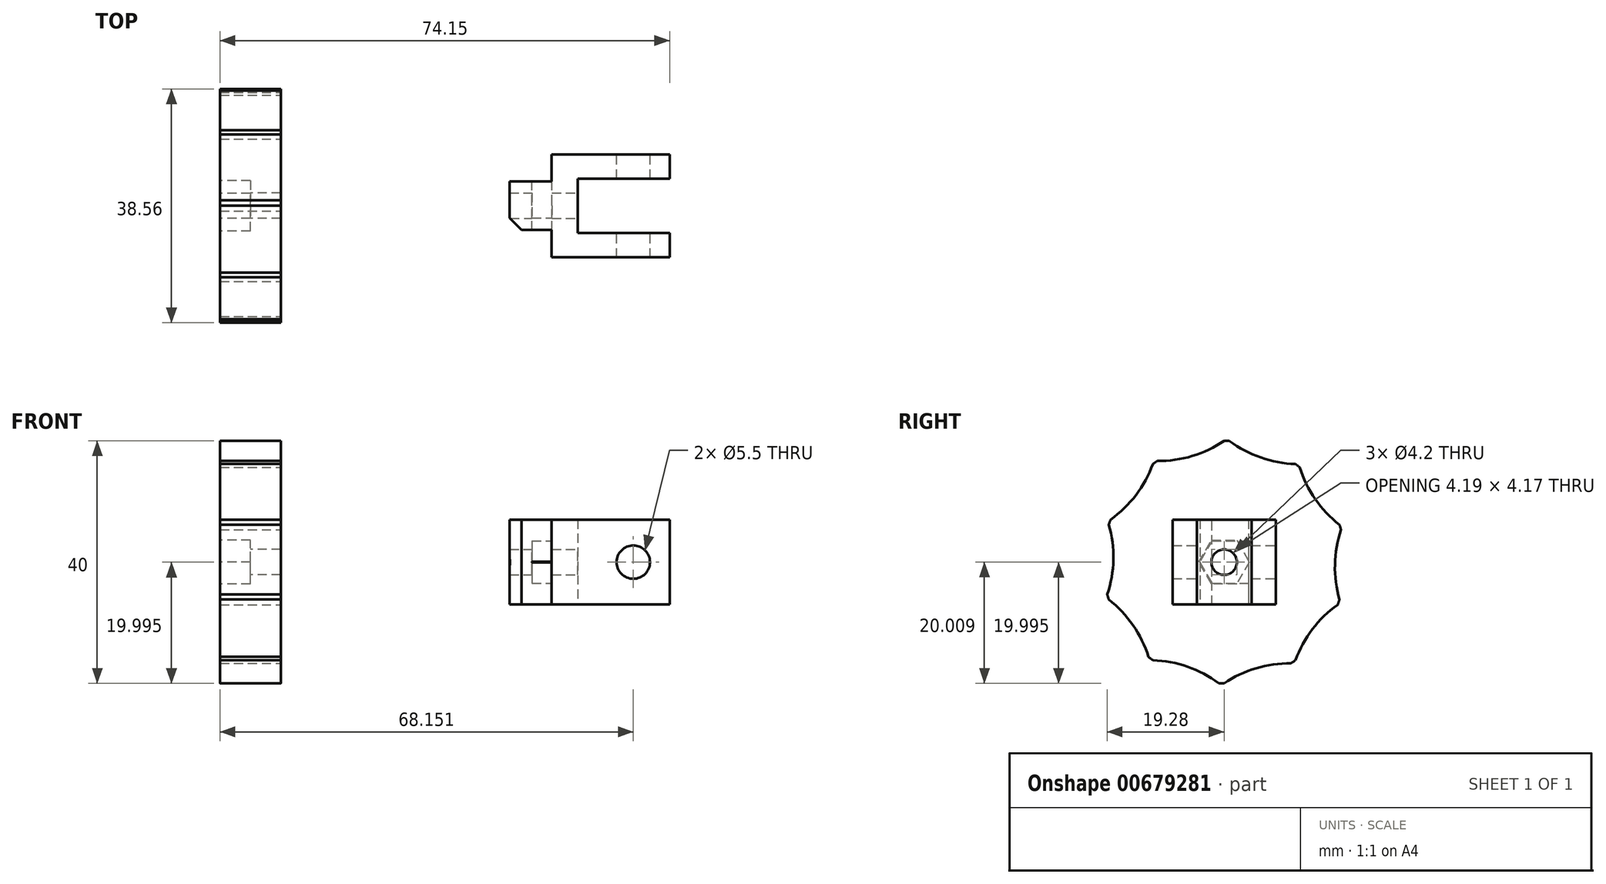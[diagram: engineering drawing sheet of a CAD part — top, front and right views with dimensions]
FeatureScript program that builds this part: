
annotation { "Feature Type Name" : "Feature", "Feature Type Description" : "" }
export const myFeature = defineFeature(function(context is Context, id is Id, definition is map)
    precondition{}
    {
        {
            var Q0;
            Q0=qCreatedBy(makeId("Front.planeOp"),FACE);
            var sketch = newSketch(context, id + "F0", { "sketchPlane" : qUnion([Q0])});
            skLineSegment(sketch, "E0.0", {"start": v(92.84, 43.83) * mm, "end": v(42.44, 43.83) * mm, "construction": true});
            skLineSegment(sketch, "E1.0", {"start": v(54.65, 65.24) * mm, "end": v(54.65, 22.24) * mm});
            skLineSegment(sketch, "E2.bottom", {"start": v(54.65, 50.83) * mm, "end": v(74.15, 50.83) * mm});
            skLineSegment(sketch, "E2.top", {"start": v(54.65, 36.83) * mm, "end": v(74.15, 36.83) * mm});
            skLineSegment(sketch, "E2.left", {"start": v(54.65, 50.83) * mm, "end": v(54.65, 36.83) * mm});
            skLineSegment(sketch, "E2.right", {"start": v(74.15, 50.83) * mm, "end": v(74.15, 36.83) * mm});
            skFitSpline(sketch, "E3.0", {"points": [v(76.65, 67.24) * mm, v(76.65, 52.24) * mm, v(76.65, 37.24) * mm, v(76.65, 22.24) * mm]});
            skPoint(sketch, "E4.0", {"position": v(32.65, 42.74) * mm});
            skLineSegment(sketch, "E5", {"start": v(32.65, -1.43) * mm, "end": v(32.65, 77.94) * mm, "construction": true});
            skCircle(sketch, "E6", {"center": v(68.15, 43.83) * mm, "radius": 2.75 * mm});
            skCircle(sketch, "E7", {"center": v(68.15, 43.83) * mm, "radius": 9 * mm, "construction": true});
            skLineSegment(sketch, "E8", {"start": v(58.96, 50.83) * mm, "end": v(58.96, 36.83) * mm});
            skLineSegment(sketch, "E9.bottom", {"start": v(54.65, 50.83) * mm, "end": v(47.74, 50.83) * mm});
            skLineSegment(sketch, "E9.top", {"start": v(54.65, 36.83) * mm, "end": v(47.74, 36.83) * mm});
            skLineSegment(sketch, "E9.right", {"start": v(47.74, 50.83) * mm, "end": v(47.74, 36.83) * mm});
            skSolve(sketch);
        }
        {
            var Q0;
            Q0=makeQuery(id+"F0.imprint","IMPRINT",FACE,{"disambiguationData":[TD([[makeQuery(id+"F0.imprint","IMPRINT",EDGE,{"derivedFrom":sQuery(id+"F0.wireOp",EDGE,"E2.bottom")}),-1.0]])]});
            var Q1;
            {var subQ0=sQuery(id+"F0.wireOp",EDGE,"E2.right");Q1=makeQuery(id+"F0.imprint","IMPRINT",FACE,{"disambiguationData":[TD([[makeQuery(id+"F0.imprint","IMPRINT",EDGE,{"derivedFrom":subQ0}),-1.0]])]});}
            extrude(context, id + "F1", {"entities" : qUnion([Q0, Q1]), "endBound" : BoundingType.SYMMETRIC, "depth" : 17 * mm, "offsetDistance" : 25 * mm});
        }
        {
            var Q0;
            {var subQ0=sQuery(id+"F0.wireOp",EDGE,"E2.right");Q0=makeQuery(id+"F0.imprint","IMPRINT",FACE,{"disambiguationData":[TD([[makeQuery(id+"F0.imprint","IMPRINT",EDGE,{"derivedFrom":subQ0}),-1.0]])]});}
            extrude(context, id + "F2", {"entities" : qUnion([Q0]), "operationType" : NewBodyOperationType.REMOVE, "endBound" : BoundingType.SYMMETRIC, "depth" : 9 * mm, "offsetDistance" : 25 * mm});
        }
        {
            var Q0;
            Q0=makeQuery(id+"F0.imprint","IMPRINT",FACE,{"disambiguationData":[TD([[makeQuery(id+"F0.imprint","IMPRINT",EDGE,{"derivedFrom":sQuery(id+"F0.wireOp",EDGE,"E9.bottom")}),1.0]])]});
            extrude(context, id + "F3", {"entities" : qUnion([Q0]), "operationType" : NewBodyOperationType.ADD, "endBound" : BoundingType.SYMMETRIC, "depth" : 8 * mm, "offsetDistance" : 25 * mm});
        }
        {
            var Q0;
            Q0=makeQuery(id+"F3.opExtrude","SWEPT_FACE",FACE,{"disambiguationData":[OSD([sQuery(id+"F0.wireOp",EDGE,"E9.right")])]});
            cPlane(context, id + "F4", {"entities" : qUnion([Q0]), "cplaneType" : CPlaneType.OFFSET, "offset" : 7 * mm, "oppositeDirection" : true, "width" : 150 * mm, "height" : 150 * mm});
        }
        {
            var Q0;
            Q0=qCreatedBy(id+"F4.planeOp",FACE);
            var sketch = newSketch(context, id + "F5", { "sketchPlane" : qUnion([Q0])});
            skPoint(sketch, "E10.0", {"position": v(0, 43.83) * mm});
            skCircle(sketch, "E11.cCircle", {"center": v(0, 43.83) * mm, "radius": 3.5 * mm, "construction": true});
            skLineSegment(sketch, "E11.0", {"start": v(-2.02, 47.33) * mm, "end": v(2.02, 47.33) * mm});
            skLineSegment(sketch, "E11.1", {"start": v(2.02, 47.33) * mm, "end": v(4.04, 43.83) * mm});
            skLineSegment(sketch, "E11.2", {"start": v(4.04, 43.83) * mm, "end": v(2.02, 40.33) * mm});
            skLineSegment(sketch, "E11.3", {"start": v(2.02, 40.33) * mm, "end": v(-4, 40.33) * mm});
            skPoint(sketch, "E11.0.midPoint", {"position": v(0, 47.33) * mm});
            skCircle(sketch, "E12", {"center": v(0, 43.83) * mm, "radius": 2.1 * mm});
            skLineSegment(sketch, "E13.0", {"start": v(-4, 50.83) * mm, "end": v(-4, 36.83) * mm});
            skLineSegment(sketch, "E14", {"start": v(-2.02, 47.33) * mm, "end": v(-4, 47.33) * mm});
            skSolve(sketch);
        }
        {
            var Q0;
            Q0=qSketchRegion(id+"F5",true);
            extrude(context, id + "F6", {"entities" : qUnion([Q0]), "operationType" : NewBodyOperationType.REMOVE, "depth" : 3.3 * mm, "offsetDistance" : 25 * mm});
        }
        {
            var Q0;
            Q0=makeQuery(id+"F5.imprint","IMPRINT",FACE,{"disambiguationData":[TD([[makeQuery(id+"F5.imprint","IMPRINT",EDGE,{"derivedFrom":sQuery(id+"F5.wireOp",EDGE,"E12")}),1.0]])]});
            extrude(context, id + "F7", {"entities" : qUnion([Q0]), "operationType" : NewBodyOperationType.REMOVE, "endBound" : BoundingType.SYMMETRIC, "depth" : 14.6 * mm, "offsetDistance" : 25 * mm});
        }
        {
            var Q0;
            Q0=makeQuery(id+"F3.opExtrude","CAP_EDGE",EDGE,{"disambiguationData":[OSD([sQuery(id+"F0.wireOp",EDGE,"E9.right")])],"isStart":false});
            chamfer(context, id + "F8", {"entities" : qUnion([Q0]), "width" : 2 * mm, "tangentPropagation" : true});
        }
        {
            var Q0;
            Q0=qCreatedBy(makeId("Right.planeOp"),FACE);
            var sketch = newSketch(context, id + "F9", { "sketchPlane" : qUnion([Q0])});
            skPoint(sketch, "E15.0", {"position": v(0, 43.83) * mm});
            skPoint(sketch, "E15.1", {"position": v(0, 47.33) * mm});
            skCircle(sketch, "E16", {"center": v(0, 43.83) * mm, "radius": 2.1 * mm});
            skCircle(sketch, "E17", {"center": v(0, 43.83) * mm, "radius": 20 * mm});
            skCircle(sketch, "E18.cCircle", {"center": v(0, 43.83) * mm, "radius": 3.6 * mm, "construction": true});
            skLineSegment(sketch, "E18.0", {"start": v(-2.08, 47.43) * mm, "end": v(2.08, 47.43) * mm});
            skLineSegment(sketch, "E18.1", {"start": v(2.08, 47.43) * mm, "end": v(4.16, 43.83) * mm});
            skLineSegment(sketch, "E18.2", {"start": v(4.16, 43.83) * mm, "end": v(2.08, 40.23) * mm});
            skLineSegment(sketch, "E18.3", {"start": v(2.08, 40.23) * mm, "end": v(-2.08, 40.23) * mm});
            skLineSegment(sketch, "E18.4", {"start": v(-2.08, 40.23) * mm, "end": v(-4.16, 43.83) * mm});
            skLineSegment(sketch, "E18.5", {"start": v(-4.16, 43.83) * mm, "end": v(-2.08, 47.43) * mm});
            skPoint(sketch, "E18.0.midPoint", {"position": v(0, 47.43) * mm});
            skSolve(sketch);
        }
        {
            var Q0;
            Q0=qSketchRegion(id+"F9",true);
            var Q1;
            Q1=makeQuery(id+"F9.imprint","IMPRINT",FACE,{"disambiguationData":[TD([[makeQuery(id+"F9.imprint","IMPRINT",EDGE,{"derivedFrom":sQuery(id+"F9.wireOp",EDGE,"E16")}),-1.0]])]});
            var Q2;
            Q2=makeQuery(id+"F9.imprint","IMPRINT",FACE,{"disambiguationData":[TD([[makeQuery(id+"F9.imprint","IMPRINT",EDGE,{"derivedFrom":sQuery(id+"F9.wireOp",EDGE,"4015ee51-9cf9-47a1-a58a-391af3ff6af4.0")}),-1.0]])]});
            extrude(context, id + "F10", {"entities" : qUnion([Q0, Q1, Q2]), "depth" : 10 * mm, "offsetDistance" : 25 * mm});
        }
        {
            var Q0;
            Q0=makeQuery(id+"F9.imprint","IMPRINT",FACE,{"disambiguationData":[TD([[makeQuery(id+"F9.imprint","IMPRINT",EDGE,{"derivedFrom":sQuery(id+"F9.wireOp",EDGE,"E16")}),-1.0]])]});
            var Q1;
            Q1=makeQuery(id+"F9.imprint","IMPRINT",FACE,{"disambiguationData":[TD([[makeQuery(id+"F9.imprint","IMPRINT",EDGE,{"derivedFrom":sQuery(id+"F9.wireOp",EDGE,"4015ee51-9cf9-47a1-a58a-391af3ff6af4.0")}),-1.0]])]});
            extrude(context, id + "F11", {"entities" : qUnion([Q0, Q1]), "operationType" : NewBodyOperationType.REMOVE, "depth" : 5 * mm, "offsetDistance" : 25 * mm});
        }
        {
            var Q0;
            Q0=makeQuery(id+"F9.imprint","IMPRINT",FACE,{"disambiguationData":[TD([[makeQuery(id+"F9.imprint","IMPRINT",EDGE,{"derivedFrom":sQuery(id+"F9.wireOp",EDGE,"4015ee51-9cf9-47a1-a58a-391af3ff6af4.0")}),1.0]])]});
            var Q1;
            Q1=makeQuery(id+"F9.imprint","IMPRINT",FACE,{"disambiguationData":[TD([[makeQuery(id+"F9.imprint","IMPRINT",EDGE,{"derivedFrom":sQuery(id+"F9.wireOp",EDGE,"E17")}),1.0]])]});
            cPlane(context, id + "F12", {"entities" : qUnion([Q0, Q1]), "cplaneType" : CPlaneType.OFFSET, "offset" : 10 * mm, "width" : 150 * mm, "height" : 150 * mm});
        }
        {
            var Q0;
            Q0=qCreatedBy(id+"F12.planeOp",FACE);
            var sketch = newSketch(context, id + "F13", { "sketchPlane" : qUnion([Q0])});
            skCircle(sketch, "E19.0", {"center": v(0, 43.83) * mm, "radius": 20 * mm});
            skPoint(sketch, "E19.1", {"position": v(0, 43.83) * mm});
            skLineSegment(sketch, "E20", {"start": v(0, 43.83) * mm, "end": v(0, 63.83) * mm, "construction": true});
            skLineSegment(sketch, "E21", {"start": v(-11.02, 60.51) * mm, "end": v(0, 43.83) * mm, "construction": true});
            skArc(sketch, "E22", {"start": v(-11.02, 60.51) * mm, "mid": v(-5.26, 61.33) * mm, "end": v(0, 63.83) * mm});
            skArc(sketch, "E23.1.0", {"start": v(-18.73, 50.85) * mm, "mid": v(-14.54, 54.9) * mm, "end": v(-11.76, 60) * mm});
            skArc(sketch, "E23.2.0", {"start": v(-19.28, 38.5) * mm, "mid": v(-18.27, 44.23) * mm, "end": v(-19.02, 50) * mm});
            skArc(sketch, "E23.3.0", {"start": v(-12.47, 28.19) * mm, "mid": v(-15.02, 33.41) * mm, "end": v(-19.02, 37.64) * mm});
            skArc(sketch, "E23.4.0", {"start": v(-0.9, 23.85) * mm, "mid": v(-6.04, 26.57) * mm, "end": v(-11.76, 27.64) * mm});
            skArc(sketch, "E23.5.0", {"start": v(11.02, 27.14) * mm, "mid": v(5.26, 26.32) * mm, "end": v(0, 23.83) * mm});
            skArc(sketch, "E23.6.0", {"start": v(18.73, 36.8) * mm, "mid": v(14.54, 32.75) * mm, "end": v(11.76, 27.64) * mm});
            skArc(sketch, "E23.7.0", {"start": v(19.28, 49.15) * mm, "mid": v(18.27, 43.42) * mm, "end": v(19.02, 37.64) * mm});
            skArc(sketch, "E23.8.0", {"start": v(12.47, 59.46) * mm, "mid": v(15.02, 54.24) * mm, "end": v(19.02, 50) * mm});
            skArc(sketch, "E23.9.0", {"start": v(0.9, 63.8) * mm, "mid": v(6.04, 61.08) * mm, "end": v(11.76, 60) * mm});
            skCircle(sketch, "E24", {"center": v(0, 43.83) * mm, "radius": 10 * mm});
            skSolve(sketch);
        }
        {
            var Q0;
            {var subQ0=sQuery(id+"F13.wireOp",EDGE,"E23.8.0");Q0=makeQuery(id+"F13.imprint","IMPRINT",FACE,{"disambiguationData":[TD([[makeQuery(id+"F13.imprint","IMPRINT",EDGE,{"derivedFrom":subQ0}),1.0]])]});}
            var Q1;
            {var subQ0=sQuery(id+"F13.wireOp",EDGE,"E23.9.0");Q1=makeQuery(id+"F13.imprint","IMPRINT",FACE,{"disambiguationData":[TD([[makeQuery(id+"F13.imprint","IMPRINT",EDGE,{"derivedFrom":subQ0}),1.0]])]});}
            var Q2;
            {var subQ0=sQuery(id+"F13.wireOp",EDGE,"E22");Q2=makeQuery(id+"F13.imprint","IMPRINT",FACE,{"disambiguationData":[TD([[makeQuery(id+"F13.imprint","IMPRINT",EDGE,{"derivedFrom":subQ0}),1.0]])]});}
            var Q3;
            {var subQ0=sQuery(id+"F13.wireOp",EDGE,"E23.1.0");Q3=makeQuery(id+"F13.imprint","IMPRINT",FACE,{"disambiguationData":[TD([[makeQuery(id+"F13.imprint","IMPRINT",EDGE,{"derivedFrom":subQ0}),1.0]])]});}
            var Q4;
            {var subQ0=sQuery(id+"F13.wireOp",EDGE,"E23.2.0");Q4=makeQuery(id+"F13.imprint","IMPRINT",FACE,{"disambiguationData":[TD([[makeQuery(id+"F13.imprint","IMPRINT",EDGE,{"derivedFrom":subQ0}),1.0]])]});}
            var Q5;
            {var subQ0=sQuery(id+"F13.wireOp",EDGE,"E23.3.0");Q5=makeQuery(id+"F13.imprint","IMPRINT",FACE,{"disambiguationData":[TD([[makeQuery(id+"F13.imprint","IMPRINT",EDGE,{"derivedFrom":subQ0}),1.0]])]});}
            var Q6;
            {var subQ0=sQuery(id+"F13.wireOp",EDGE,"E23.4.0");Q6=makeQuery(id+"F13.imprint","IMPRINT",FACE,{"disambiguationData":[TD([[makeQuery(id+"F13.imprint","IMPRINT",EDGE,{"derivedFrom":subQ0}),1.0]])]});}
            var Q7;
            {var subQ0=sQuery(id+"F13.wireOp",EDGE,"E23.5.0");Q7=makeQuery(id+"F13.imprint","IMPRINT",FACE,{"disambiguationData":[TD([[makeQuery(id+"F13.imprint","IMPRINT",EDGE,{"derivedFrom":subQ0}),1.0]])]});}
            var Q8;
            {var subQ0=sQuery(id+"F13.wireOp",EDGE,"E23.6.0");Q8=makeQuery(id+"F13.imprint","IMPRINT",FACE,{"disambiguationData":[TD([[makeQuery(id+"F13.imprint","IMPRINT",EDGE,{"derivedFrom":subQ0}),1.0]])]});}
            var Q9;
            {var subQ0=sQuery(id+"F13.wireOp",EDGE,"E23.7.0");Q9=makeQuery(id+"F13.imprint","IMPRINT",FACE,{"disambiguationData":[TD([[makeQuery(id+"F13.imprint","IMPRINT",EDGE,{"derivedFrom":subQ0}),1.0]])]});}
            var Q10;
            Q10=makeQuery(id+"F13.imprint","IMPRINT",FACE,{"disambiguationData":[TD([[makeQuery(id+"F13.imprint","IMPRINT",EDGE,{"derivedFrom":makeQuery(id+"F9.imprint","IMPRINT",EDGE,{"derivedFrom":sQuery(id+"F9.wireOp",EDGE,"4015ee51-9cf9-47a1-a58a-391af3ff6af4.0")})}),-1.0]])]});
            extrude(context, id + "F14", {"entities" : qUnion([Q0, Q1, Q2, Q3, Q4, Q5, Q6, Q7, Q8, Q9, Q10]), "operationType" : NewBodyOperationType.REMOVE, "oppositeDirection" : true, "depth" : 25 * mm, "offsetDistance" : 25 * mm});
        }
    });
